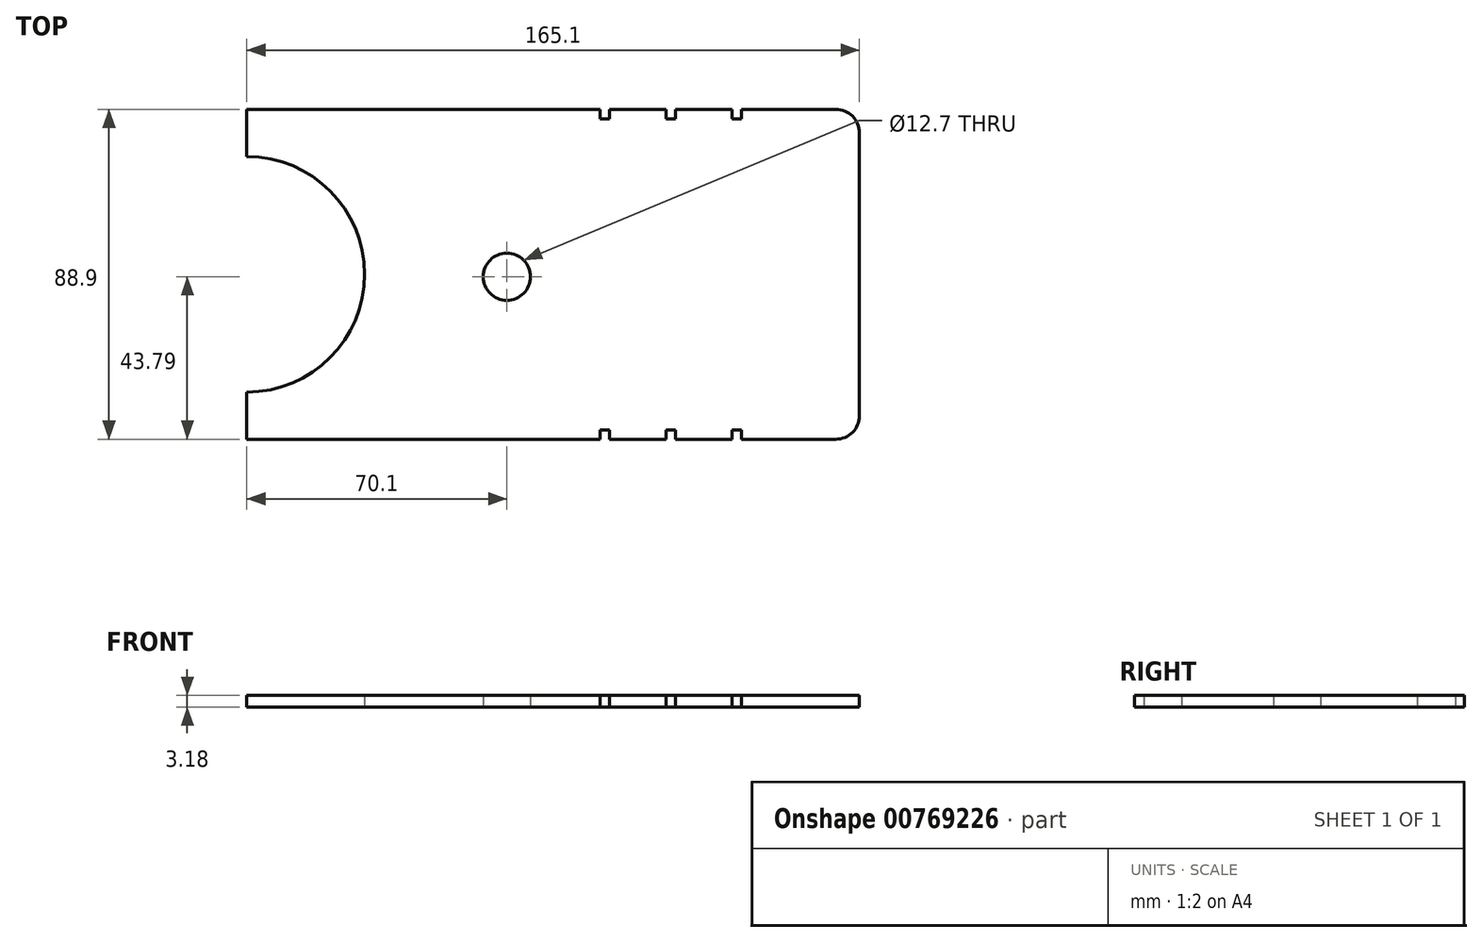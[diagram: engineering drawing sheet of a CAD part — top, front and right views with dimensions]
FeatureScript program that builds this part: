
annotation { "Feature Type Name" : "Feature", "Feature Type Description" : "" }
export const myFeature = defineFeature(function(context is Context, id is Id, definition is map)
    precondition{}
    {
        {
            var Q0;
            Q0=qCreatedBy(makeId("Top.planeOp"),FACE);
            var sketch = newSketch(context, id + "F0", { "sketchPlane" : qUnion([Q0])});
            skLineSegment(sketch, "E0.bottom", {"start": v(75.95, -43.79) * mm, "end": v(-38.35, -43.79) * mm});
            skLineSegment(sketch, "E0.top", {"start": v(75.95, 45.11) * mm, "end": v(-38.35, 45.11) * mm});
            skLineSegment(sketch, "E0.left", {"start": v(82.3, -37.44) * mm, "end": v(82.3, 38.76) * mm});
            skPoint(sketch, "E0.middle", {"position": v(0, 0) * mm});
            skPoint(sketch, "E1.visualSharp", {"position": v(82.3, 45.11) * mm});
            skArc(sketch, "E1.filletArc", {"start": v(82.3, 38.76) * mm, "mid": v(80.44, 43.25) * mm, "end": v(75.95, 45.11) * mm});
            skPoint(sketch, "E2.visualSharp", {"position": v(82.3, -43.79) * mm});
            skArc(sketch, "E2.filletArc", {"start": v(75.95, -43.79) * mm, "mid": v(80.44, -41.93) * mm, "end": v(82.3, -37.44) * mm});
            skCircle(sketch, "E3", {"center": v(-12.7, 0) * mm, "radius": 6.35 * mm});
            skLineSegment(sketch, "E4.bottom", {"start": v(30.23, 45.11) * mm, "end": v(32.77, 45.11) * mm});
            skLineSegment(sketch, "E4.top", {"start": v(30.23, 42.57) * mm, "end": v(32.77, 42.57) * mm});
            skLineSegment(sketch, "E4.left", {"start": v(30.23, 45.11) * mm, "end": v(30.23, 42.57) * mm});
            skLineSegment(sketch, "E4.right", {"start": v(32.77, 45.11) * mm, "end": v(32.77, 42.57) * mm});
            skLineSegment(sketch, "E5.bottom", {"start": v(30.23, -43.79) * mm, "end": v(32.77, -43.79) * mm});
            skLineSegment(sketch, "E5.top", {"start": v(30.23, -41.25) * mm, "end": v(32.77, -41.25) * mm});
            skLineSegment(sketch, "E5.left", {"start": v(30.23, -43.79) * mm, "end": v(30.23, -41.25) * mm});
            skLineSegment(sketch, "E5.right", {"start": v(32.77, -43.79) * mm, "end": v(32.77, -41.25) * mm});
            skLineSegment(sketch, "E6", {"start": v(-38.35, 45.11) * mm, "end": v(-38.35, -43.79) * mm});
            skPoint(sketch, "E7.middle", {"position": v(34.24, 0) * mm});
            skLineSegment(sketch, "E8.bottom", {"start": v(12.45, 45.11) * mm, "end": v(14.99, 45.11) * mm});
            skLineSegment(sketch, "E8.top", {"start": v(12.45, 42.57) * mm, "end": v(14.99, 42.57) * mm});
            skLineSegment(sketch, "E8.left", {"start": v(12.45, 45.11) * mm, "end": v(12.45, 42.57) * mm});
            skLineSegment(sketch, "E8.right", {"start": v(14.99, 45.11) * mm, "end": v(14.99, 42.57) * mm});
            skLineSegment(sketch, "E9.bottom", {"start": v(48, 45.11) * mm, "end": v(50.55, 45.11) * mm});
            skLineSegment(sketch, "E9.top", {"start": v(48, 42.57) * mm, "end": v(50.55, 42.57) * mm});
            skLineSegment(sketch, "E9.left", {"start": v(48, 45.11) * mm, "end": v(48, 42.57) * mm});
            skLineSegment(sketch, "E9.right", {"start": v(50.55, 45.11) * mm, "end": v(50.55, 42.57) * mm});
            skLineSegment(sketch, "E10.bottom", {"start": v(12.45, -43.79) * mm, "end": v(14.99, -43.79) * mm});
            skLineSegment(sketch, "E10.top", {"start": v(12.45, -41.25) * mm, "end": v(14.99, -41.25) * mm});
            skLineSegment(sketch, "E10.left", {"start": v(12.45, -43.79) * mm, "end": v(12.45, -41.25) * mm});
            skLineSegment(sketch, "E10.right", {"start": v(14.99, -43.79) * mm, "end": v(14.99, -41.25) * mm});
            skLineSegment(sketch, "E11.bottom", {"start": v(48, -43.79) * mm, "end": v(50.55, -43.79) * mm});
            skLineSegment(sketch, "E11.top", {"start": v(48, -41.25) * mm, "end": v(50.55, -41.25) * mm});
            skLineSegment(sketch, "E11.left", {"start": v(48, -43.79) * mm, "end": v(48, -41.25) * mm});
            skLineSegment(sketch, "E11.right", {"start": v(50.55, -43.79) * mm, "end": v(50.55, -41.25) * mm});
            skLineSegment(sketch, "E12.bottom", {"start": v(-38.35, 45.11) * mm, "end": v(-82.8, 45.11) * mm});
            skLineSegment(sketch, "E12.top", {"start": v(-38.35, -43.79) * mm, "end": v(-82.8, -43.79) * mm});
            skLineSegment(sketch, "E12.right", {"start": v(-82.8, 45.11) * mm, "end": v(-82.8, -43.79) * mm});
            skArc(sketch, "E13", {"start": v(-82.8, -31.09) * mm, "mid": v(-51.05, 0.66) * mm, "end": v(-82.8, 32.41) * mm});
            skSolve(sketch);
        }
        {
            var Q0;
            Q0=makeQuery(id+"F0.imprint","IMPRINT",FACE,{"disambiguationData":[TD([[makeQuery(id+"F0.imprint","IMPRINT",EDGE,{"derivedFrom":sQuery(id+"F0.wireOp",EDGE,"E0.bottom")}),-1.0]])]});
            var Q1;
            Q1=makeQuery(id+"F0.imprint","IMPRINT",FACE,{"disambiguationData":[TD([[makeQuery(id+"F0.imprint","IMPRINT",EDGE,{"derivedFrom":sQuery(id+"F0.wireOp",EDGE,"ff9ab77d-f841-4422-bed5-9a21e7365881.filletArc")}),1.0]])]});
            var Q2;
            Q2=makeQuery(id+"F0.imprint","IMPRINT",FACE,{"disambiguationData":[TD([[makeQuery(id+"F0.imprint","IMPRINT",EDGE,{"derivedFrom":sQuery(id+"F0.wireOp",EDGE,"E12.bottom")}),1.0]])]});
            extrude(context, id + "F1", {"entities" : qUnion([Q0, Q1, Q2]), "depth" : 3.17 * mm, "offsetDistance" : 25.4 * mm});
        }
    });
